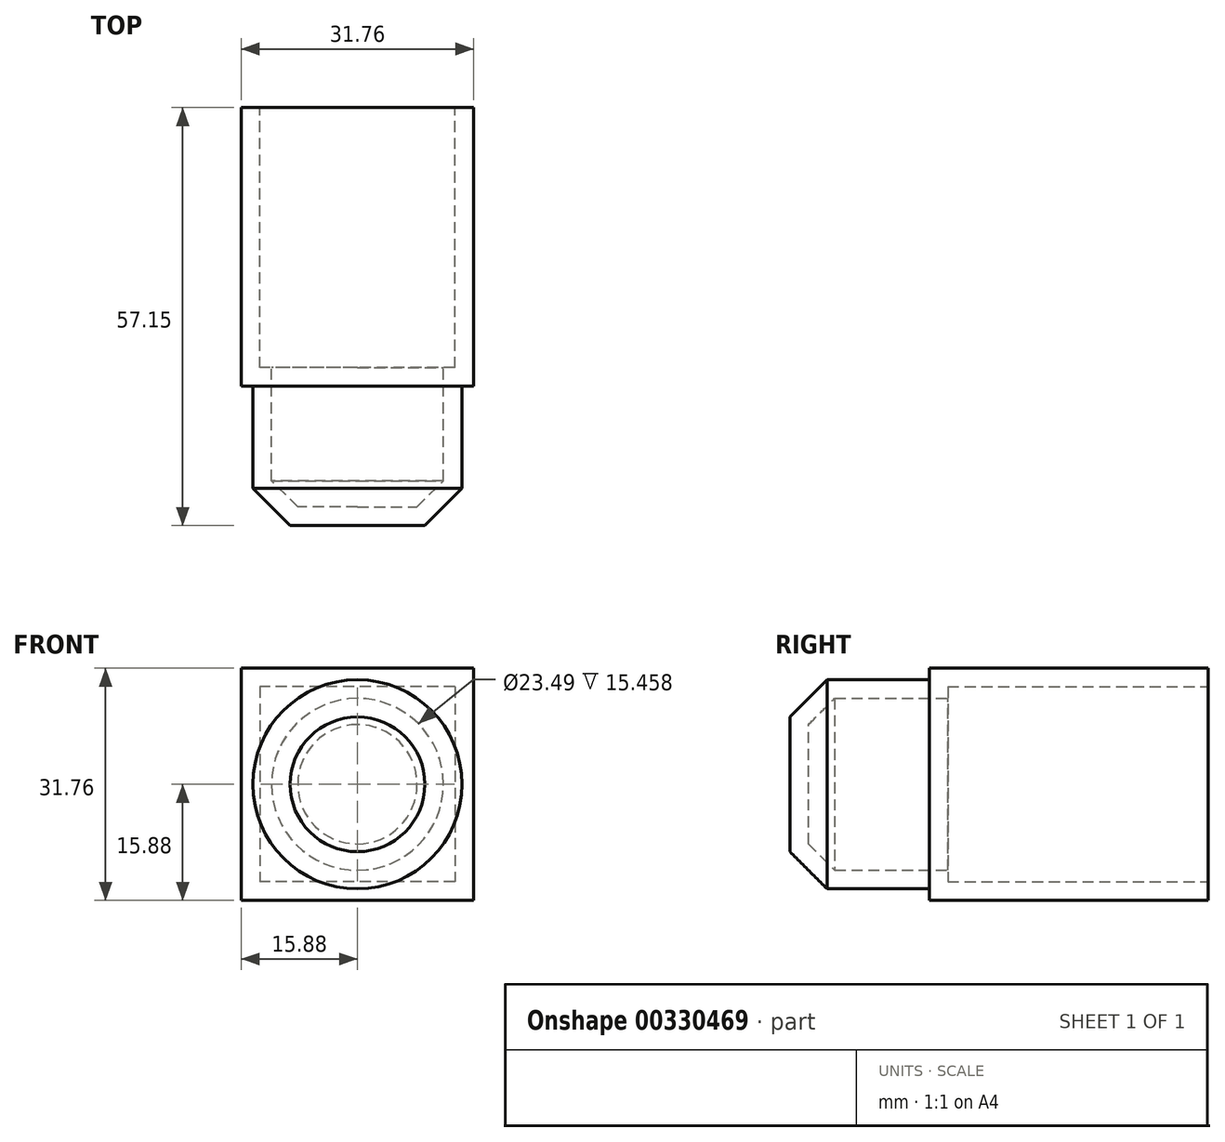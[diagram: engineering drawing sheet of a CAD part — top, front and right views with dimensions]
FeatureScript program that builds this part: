
annotation { "Feature Type Name" : "Feature", "Feature Type Description" : "" }
export const myFeature = defineFeature(function(context is Context, id is Id, definition is map)
    precondition{}
    {
        {
            var Q0;
            Q0=qCreatedBy(makeId("Front.planeOp"),FACE);
            var sketch = newSketch(context, id + "F0", { "sketchPlane" : qUnion([Q0])});
            skLineSegment(sketch, "E0.bottom", {"start": v(15.88, 15.87) * mm, "end": v(-15.87, 15.87) * mm});
            skLineSegment(sketch, "E0.top", {"start": v(15.87, -15.88) * mm, "end": v(-15.88, -15.88) * mm});
            skLineSegment(sketch, "E0.left", {"start": v(15.88, 15.87) * mm, "end": v(15.87, -15.88) * mm});
            skLineSegment(sketch, "E0.right", {"start": v(-15.87, 15.87) * mm, "end": v(-15.88, -15.88) * mm});
            skPoint(sketch, "E0.middle", {"position": v(0, 0) * mm});
            skSolve(sketch);
        }
        {
            var Q0;
            Q0=qSketchRegion(id+"F0",true);
            extrude(context, id + "F1", {"entities" : qUnion([Q0]), "depth" : 38.1 * mm, "symmetric" : true});
        }
        {
            var Q0;
            Q0=makeQuery(id+"F1.opExtrude","CAP_FACE",FACE,{"disambiguationData":[OSD([sQuery(id+"F0.wireOp",EDGE,"E0.bottom"),sQuery(id+"F0.wireOp",EDGE,"E0.top"),sQuery(id+"F0.wireOp",EDGE,"E0.left"),sQuery(id+"F0.wireOp",EDGE,"E0.right")])],"isStart":false});
            var sketch = newSketch(context, id + "F2", { "sketchPlane" : qUnion([Q0])});
            skCircle(sketch, "E1", {"center": v(0, 0) * mm, "radius": 14.29 * mm});
            skSolve(sketch);
        }
        {
            var Q0;
            Q0=qSketchRegion(id+"F2",true);
            extrude(context, id + "F3", {"entities" : qUnion([Q0]), "operationType" : NewBodyOperationType.ADD, "depth" : 19.05 * mm});
        }
        {
            var Q0;
            Q0=makeQuery(id+"F3.opExtrude","CAP_EDGE",EDGE,{"disambiguationData":[OSD([sQuery(id+"F2.wireOp",EDGE,"E1")])],"isStart":false});
            chamfer(context, id + "F4", {"entities" : qUnion([Q0]), "width" : 5.08 * mm, "tangentPropagation" : true});
        }
        {
            var Q0;
            Q0=makeQuery(id+"F1.opExtrude","CAP_FACE",FACE,{"disambiguationData":[OSD([sQuery(id+"F0.wireOp",EDGE,"E0.bottom"),sQuery(id+"F0.wireOp",EDGE,"E0.top"),sQuery(id+"F0.wireOp",EDGE,"E0.left"),sQuery(id+"F0.wireOp",EDGE,"E0.right")])],"isStart":true});
            shell(context, id + "F5", {"entities" : qUnion([Q0]), "thickness" : 2.54 * mm});
        }
    });
